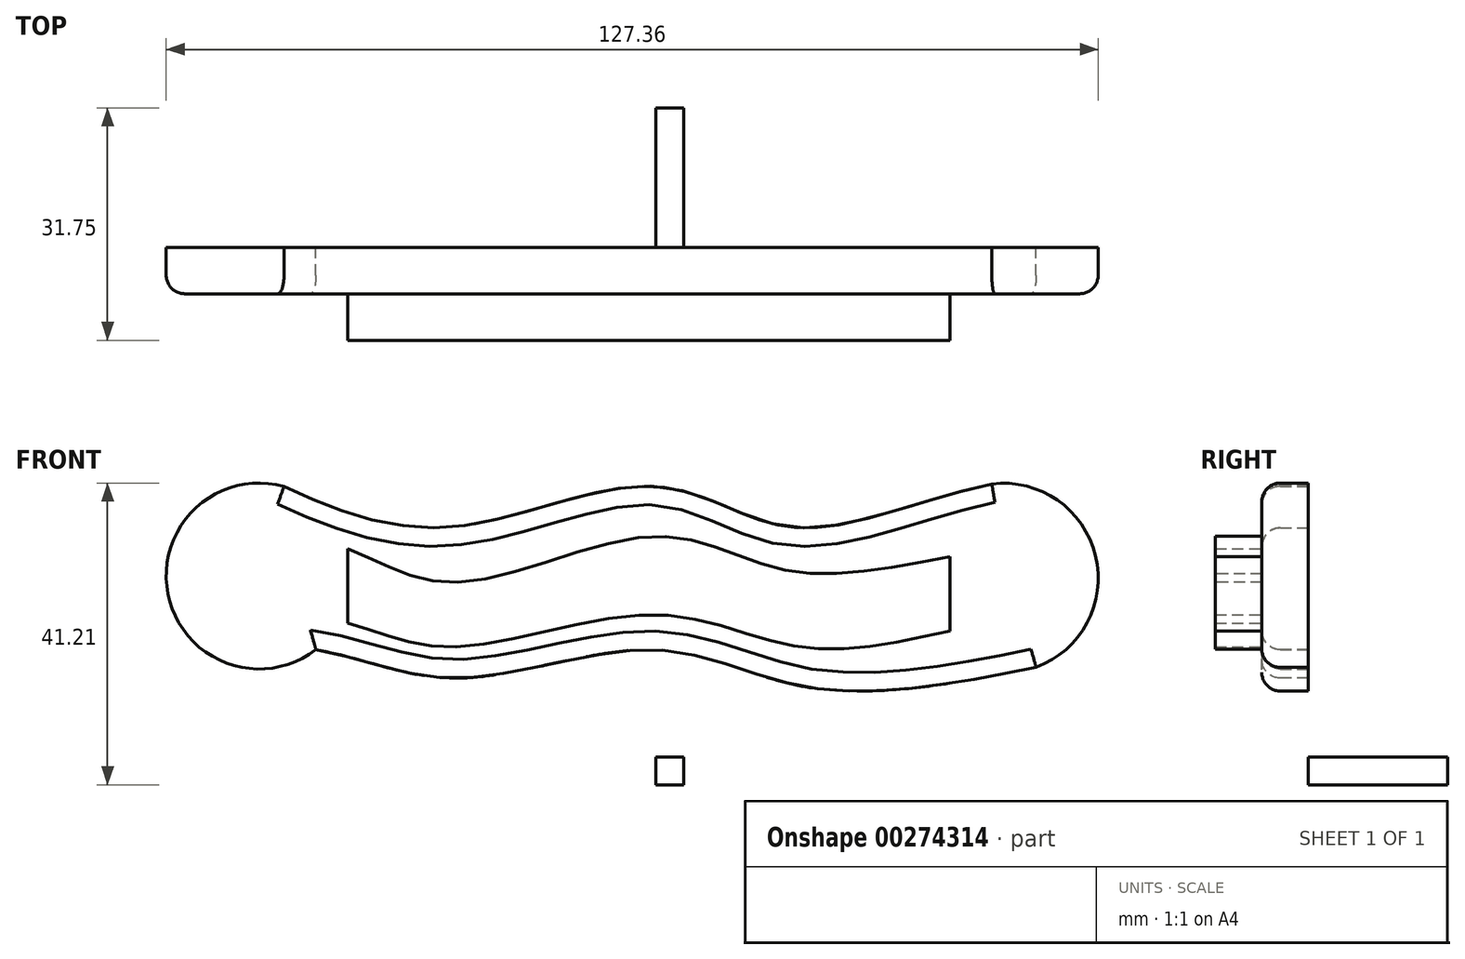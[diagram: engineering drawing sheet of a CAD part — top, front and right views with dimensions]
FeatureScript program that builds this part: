
annotation { "Feature Type Name" : "Feature", "Feature Type Description" : "" }
export const myFeature = defineFeature(function(context is Context, id is Id, definition is map)
    precondition{}
    {
        {
            var Q0;
            Q0=qCreatedBy(makeId("Front.planeOp"),FACE);
            var sketch = newSketch(context, id + "F0", { "sketchPlane" : qUnion([Q0])});
            skArc(sketch, "E0", {"start": v(-50.8, 40.74) * mm, "mid": v(-66.66, 26.08) * mm, "end": v(-46.45, 18.44) * mm});
            skArc(sketch, "E1", {"start": v(51.99, 16.04) * mm, "mid": v(60.1, 31.26) * mm, "end": v(45.92, 41.08) * mm});
            skFitSpline(sketch, "E2", {"points": [v(-50.8, 40.74) * mm, v(-27.84, 35.21) * mm, v(0, 40.74) * mm, v(18.07, 35.21) * mm, v(45.92, 41.08) * mm], "startDerivative": vector(86.64, -40.41) * mm, "endDerivative": vector(132.24, 29.83) * mm});
            skFitSpline(sketch, "E3", {"points": [v(-46.45, 18.44) * mm, v(-27.05, 14.56) * mm, v(0, 18.44) * mm, v(21.02, 13.27) * mm, v(51.99, 16.04) * mm], "startDerivative": vector(92.72, -15.8) * mm, "endDerivative": vector(110.17, 22.78) * mm});
            skLineSegment(sketch, "E4", {"start": v(-42.06, 32.23) * mm, "end": v(-42.06, 22.07) * mm});
            skLineSegment(sketch, "E5", {"start": v(40.19, 31.18) * mm, "end": v(40.19, 21.02) * mm});
            skFitSpline(sketch, "E6", {"points": [v(-42.06, 32.23) * mm, v(-27.1, 27.64) * mm, v(0, 33.92) * mm, v(17.7, 29.31) * mm, v(40.19, 31.18) * mm], "startDerivative": vector(65.05, -26.22) * mm, "endDerivative": vector(91.35, 18.2) * mm});
            skFitSpline(sketch, "E7", {"points": [v(-42.06, 22.07) * mm, v(-27.84, 18.8) * mm, v(0, 23.23) * mm, v(19.73, 18.8) * mm, v(40.19, 21.02) * mm], "startDerivative": vector(63.23, -16.78) * mm, "endDerivative": vector(84.32, 18.73) * mm});
            skSolve(sketch);
        }
        {
            var Q0;
            Q0=makeQuery(id+"F0.imprint","IMPRINT",FACE,{"disambiguationData":[TD([[makeQuery(id+"F0.imprint","IMPRINT",EDGE,{"derivedFrom":sQuery(id+"F0.wireOp",EDGE,"E0")}),1.0]])]});
            extrude(context, id + "F1", {"entities" : qUnion([Q0]), "depth" : 6.35 * mm});
        }
        {
            var Q0;
            Q0=makeQuery(id+"F0.imprint","IMPRINT",FACE,{"disambiguationData":[TD([[makeQuery(id+"F0.imprint","IMPRINT",EDGE,{"derivedFrom":sQuery(id+"F0.wireOp",EDGE,"E4")}),1.0]])]});
            extrude(context, id + "F2", {"entities" : qUnion([Q0]), "operationType" : NewBodyOperationType.ADD, "depth" : 12.7 * mm});
        }
        {
            var Q0;
            Q0=makeQuery(id+"F1.opExtrude","CAP_EDGE",EDGE,{"disambiguationData":[OSD([sQuery(id+"F0.wireOp",EDGE,"E0")])],"isStart":false});
            var Q1;
            Q1=makeQuery(id+"F1.opExtrude","CAP_EDGE",EDGE,{"disambiguationData":[OSD([sQuery(id+"F0.wireOp",EDGE,"E2")])],"isStart":false});
            var Q2;
            Q2=makeQuery(id+"F1.opExtrude","CAP_EDGE",EDGE,{"disambiguationData":[OSD([sQuery(id+"F0.wireOp",EDGE,"E3")])],"isStart":false});
            var Q3;
            Q3=makeQuery(id+"F1.opExtrude","CAP_EDGE",EDGE,{"disambiguationData":[OSD([sQuery(id+"F0.wireOp",EDGE,"E1")])],"isStart":false});
            fillet(context, id + "F3", {"entities" : qUnion([Q0, Q1, Q2, Q3]), "radius" : 2.54 * mm, "tangentPropagation" : true, "allowEdgeOverflow" : false});
        }
        {
            var Q0;
            Q0=qCreatedBy(makeId("Top.planeOp"),FACE);
            var sketch = newSketch(context, id + "F4", { "sketchPlane" : qUnion([Q0])});
            skLineSegment(sketch, "E8", {"start": v(0, 0) * mm, "end": v(0, 19.05) * mm});
            skLineSegment(sketch, "E9", {"start": v(3.81, 19.05) * mm, "end": v(0, 19.05) * mm});
            skLineSegment(sketch, "E10", {"start": v(3.81, 19.05) * mm, "end": v(3.81, 0) * mm});
            skLineSegment(sketch, "E11", {"start": v(3.81, 0) * mm, "end": v(0, 0) * mm});
            skSolve(sketch);
        }
        {
            var Q0;
            Q0 = qSketchRegion(id + "F4", true);
            extrude(context, id + "F5", {"entities" : qUnion([Q0]), "depth" : 3.8 * mm});
        }
    });
